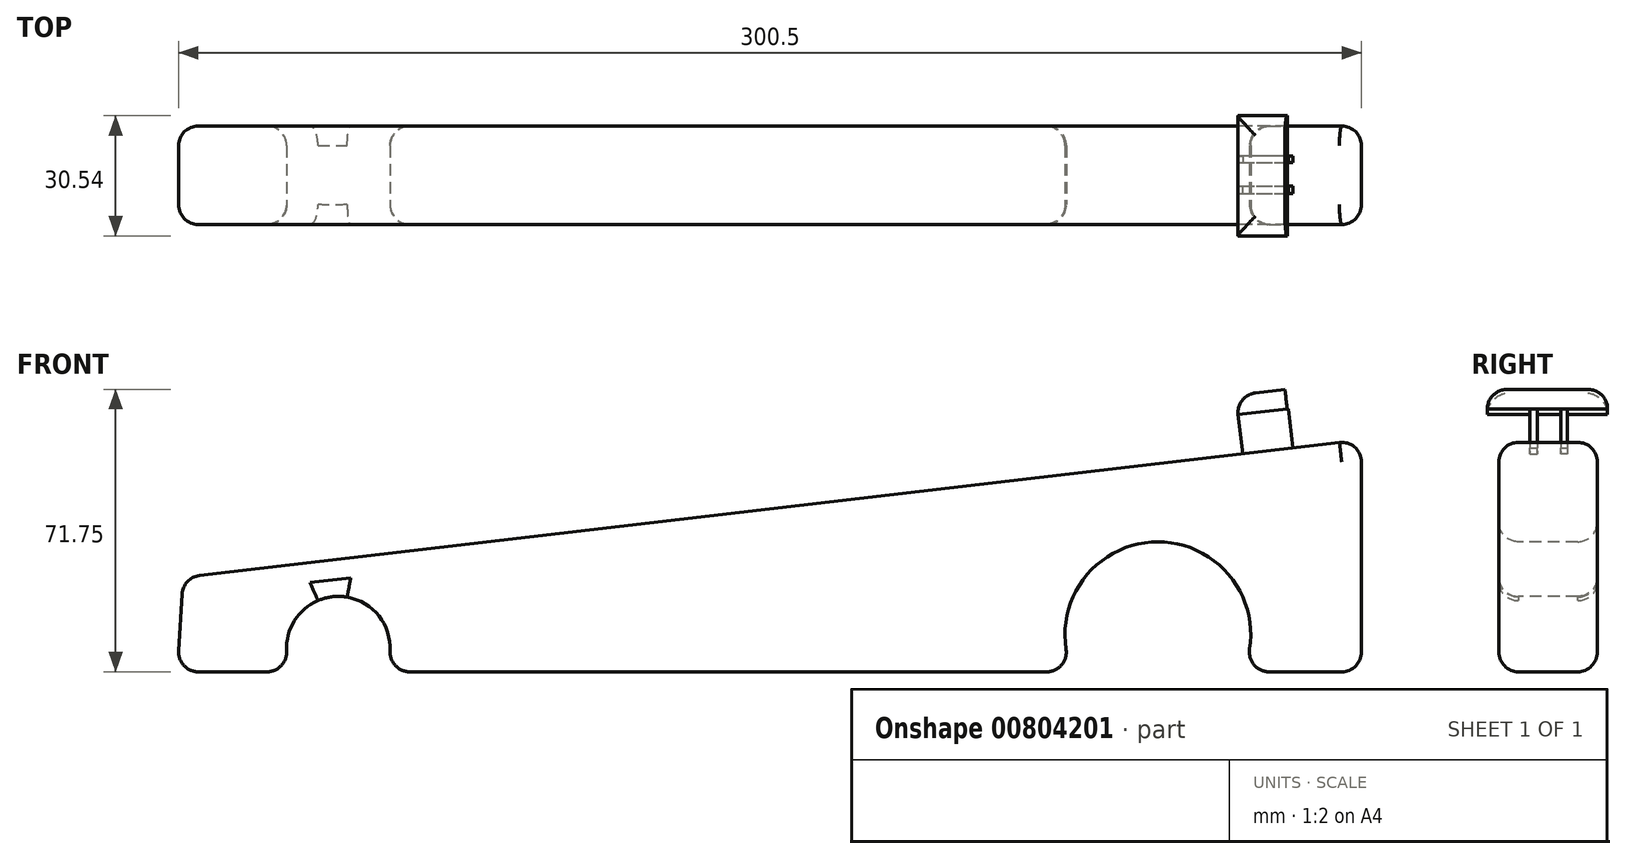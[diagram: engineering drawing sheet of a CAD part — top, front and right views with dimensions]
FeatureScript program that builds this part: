
annotation { "Feature Type Name" : "Feature", "Feature Type Description" : "" }
export const myFeature = defineFeature(function(context is Context, id is Id, definition is map)
    precondition{}
    {
        {
            var Q0;
            Q0=qCreatedBy(makeId("Front.planeOp"),FACE);
            var sketch = newSketch(context, id + "F0", { "sketchPlane" : qUnion([Q0])});
            skLineSegment(sketch, "E0", {"start": v(-173.6, -13.13) * mm, "end": v(127.2, -13.13) * mm});
            skLineSegment(sketch, "E1", {"start": v(127.2, -13.13) * mm, "end": v(127.2, 45.79) * mm});
            skLineSegment(sketch, "E2", {"start": v(127.2, 45.79) * mm, "end": v(-172.16, 10.82) * mm});
            skLineSegment(sketch, "E3", {"start": v(-172.16, 10.82) * mm, "end": v(-173.6, -13.13) * mm});
            skSolve(sketch);
        }
        {
            var Q0;
            Q0 = qSketchRegion(id + "F0", true);
            extrude(context, id + "F1", {"entities" : qUnion([Q0]), "depth" : 25 * mm, "offsetDistance" : 25 * mm});
        }
        {
            var Q0;
            Q0=makeQuery(id+"F1.opExtrude","CAP_EDGE",EDGE,{"disambiguationData":[OSD([sQuery(id+"F0.wireOp",EDGE,"E2")])],"isStart":false});
            var Q1;
            Q1=makeQuery(id+"F1.opExtrude","CAP_EDGE",EDGE,{"disambiguationData":[OSD([sQuery(id+"F0.wireOp",EDGE,"E1")])],"isStart":true});
            var Q2;
            Q2=makeQuery(id+"F1.opExtrude","CAP_EDGE",EDGE,{"disambiguationData":[OSD([sQuery(id+"F0.wireOp",EDGE,"E2")])],"isStart":true});
            var Q3;
            Q3=makeQuery(id+"F1.opExtrude","CAP_EDGE",EDGE,{"disambiguationData":[OSD([sQuery(id+"F0.wireOp",EDGE,"E1")])],"isStart":false});
            var Q4;
            Q4=makeQuery(id+"F1.opExtrude","CAP_EDGE",EDGE,{"disambiguationData":[OSD([sQuery(id+"F0.wireOp",EDGE,"E3")])],"isStart":false});
            var Q5;
            Q5=makeQuery(id+"F1.opExtrude","CAP_EDGE",EDGE,{"disambiguationData":[OSD([sQuery(id+"F0.wireOp",EDGE,"E3")])],"isStart":true});
            var Q6;
            Q6=makeQuery(id+"F1.opExtrude","SWEPT_EDGE",EDGE,{"disambiguationData":[OSD([sQuery(id+"F0.wireOp",EDGE,"E2"),sQuery(id+"F0.wireOp",EDGE,"E3")])]});
            fillet(context, id + "F2", {"entities" : qUnion([Q0, Q1, Q2, Q3, Q4, Q5, Q6]), "radius" : 5 * mm, "tangentPropagation" : true, "allowEdgeOverflow" : false});
        }
        {
            var Q0;
            Q0=makeQuery(id+"F1.opExtrude","SWEPT_EDGE",EDGE,{"disambiguationData":[OSD([sQuery(id+"F0.wireOp",EDGE,"E1"),sQuery(id+"F0.wireOp",EDGE,"E2")])]});
            fillet(context, id + "F3", {"entities" : qUnion([Q0]), "radius" : 5 * mm, "tangentPropagation" : true, "allowEdgeOverflow" : false});
        }
        {
            var Q0;
            Q0=makeQuery(id+"F1.opExtrude","CAP_FACE",FACE,{"disambiguationData":[OSD([sQuery(id+"F0.wireOp",EDGE,"E0"),sQuery(id+"F0.wireOp",EDGE,"E1"),sQuery(id+"F0.wireOp",EDGE,"E2"),sQuery(id+"F0.wireOp",EDGE,"E3")])],"isStart":false});
            var sketch = newSketch(context, id + "F4", { "sketchPlane" : qUnion([Q0])});
            skCircle(sketch, "E4", {"center": v(75.5, -3.7) * mm, "radius": 23.6 * mm});
            skCircle(sketch, "E5", {"center": v(-132.7, -7.12) * mm, "radius": 13.15 * mm});
            skSolve(sketch);
        }
        {
            var Q0;
            Q0 = qSketchRegion(id + "F4", true);
            extrude(context, id + "F5", {"entities" : qUnion([Q0]), "operationType" : NewBodyOperationType.REMOVE, "oppositeDirection" : true, "depth" : 25 * mm, "offsetDistance" : 25 * mm});
        }
        {
            var Q0;
            Q0=makeQuery(id+"F5.boolean.opBoolean","COPY",EDGE,{"derivedFrom":makeQuery(id+"F5.opExtrude","CAP_EDGE",EDGE,{"disambiguationData":[OSD([sQuery(id+"F4.wireOp",EDGE,"E5")])],"isStart":true})});
            var Q1;
            Q1=makeQuery(id+"F5.boolean.opBoolean","INTERSECT",EDGE,{"disambiguationData":[OD(0.0)],"derivedFrom":[makeQuery(id+"F1.opExtrude","SWEPT_FACE",FACE,{"disambiguationData":[OSD([sQuery(id+"F0.wireOp",EDGE,"E0")])]}),makeQuery(id+"F5.opExtrude","SWEPT_FACE",FACE,{"disambiguationData":[OSD([sQuery(id+"F4.wireOp",EDGE,"E5")])]})]});
            var Q2;
            {var subQ0=sQuery(id+"F0.wireOp",EDGE,"E0");Q2=makeQuery(id+"F5.boolean.opBoolean","SPLIT",EDGE,{"disambiguationData":[TD([makeQuery(id+"F1.opExtrude","SWEPT_FACE",FACE,{"disambiguationData":[OSD([subQ0])]}),makeQuery(id+"F1.opExtrude","CAP_FACE",FACE,{"disambiguationData":[OSD([subQ0,sQuery(id+"F0.wireOp",EDGE,"E1"),sQuery(id+"F0.wireOp",EDGE,"E2"),sQuery(id+"F0.wireOp",EDGE,"E3")])],"isStart":false}),makeQuery(id+"F5.opExtrude","SWEPT_FACE",FACE,{"disambiguationData":[OSD([sQuery(id+"F4.wireOp",EDGE,"E4")])]}),makeQuery(id+"F5.opExtrude","SWEPT_FACE",FACE,{"disambiguationData":[OSD([sQuery(id+"F4.wireOp",EDGE,"E5")])]})])],"derivedFrom":makeQuery(id+"F1.opExtrude","CAP_EDGE",EDGE,{"disambiguationData":[OSD([subQ0])],"isStart":false})});}
            var Q3;
            Q3=makeQuery(id+"F5.boolean.opBoolean","INTERSECT",EDGE,{"disambiguationData":[OD(1.0)],"derivedFrom":[makeQuery(id+"F1.opExtrude","SWEPT_FACE",FACE,{"disambiguationData":[OSD([sQuery(id+"F0.wireOp",EDGE,"E0")])]}),makeQuery(id+"F5.opExtrude","SWEPT_FACE",FACE,{"disambiguationData":[OSD([sQuery(id+"F4.wireOp",EDGE,"E4")])]})]});
            var Q4;
            Q4=makeQuery(id+"F5.boolean.opBoolean","COPY",EDGE,{"derivedFrom":makeQuery(id+"F5.opExtrude","CAP_EDGE",EDGE,{"disambiguationData":[OSD([sQuery(id+"F4.wireOp",EDGE,"E4")])],"isStart":true})});
            var Q5;
            Q5=makeQuery(id+"F5.boolean.opBoolean","INTERSECT",EDGE,{"disambiguationData":[OD(0.0)],"derivedFrom":[makeQuery(id+"F1.opExtrude","SWEPT_FACE",FACE,{"disambiguationData":[OSD([sQuery(id+"F0.wireOp",EDGE,"E0")])]}),makeQuery(id+"F5.opExtrude","SWEPT_FACE",FACE,{"disambiguationData":[OSD([sQuery(id+"F4.wireOp",EDGE,"E4")])]})]});
            var Q6;
            Q6=makeQuery(id+"F5.boolean.opBoolean","INTERSECT",EDGE,{"disambiguationData":[OD(1.0)],"derivedFrom":[makeQuery(id+"F1.opExtrude","SWEPT_FACE",FACE,{"disambiguationData":[OSD([sQuery(id+"F0.wireOp",EDGE,"E0")])]}),makeQuery(id+"F5.opExtrude","SWEPT_FACE",FACE,{"disambiguationData":[OSD([sQuery(id+"F4.wireOp",EDGE,"E5")])]})]});
            fillet(context, id + "F6", {"entities" : qUnion([Q0, Q1, Q2, Q3, Q4, Q5, Q6]), "radius" : 5 * mm, "tangentPropagation" : true, "allowEdgeOverflow" : false});
        }
        {
            var Q0;
            {var subQ0=sQuery(id+"F0.wireOp",EDGE,"E0");Q0=makeQuery(id+"F6.opFillet","BLEND_EDGE",EDGE,{"blendedFrom":[makeQuery(id+"F5.boolean.opBoolean","INTERSECT",EDGE,{"disambiguationData":[OD(0.0)],"derivedFrom":[makeQuery(id+"F1.opExtrude","SWEPT_FACE",FACE,{"disambiguationData":[OSD([subQ0])]}),makeQuery(id+"F5.opExtrude","SWEPT_FACE",FACE,{"disambiguationData":[OSD([sQuery(id+"F4.wireOp",EDGE,"E5")])]})]}),makeQuery(id+"F1.opExtrude","CAP_FACE",FACE,{"disambiguationData":[OSD([subQ0,sQuery(id+"F0.wireOp",EDGE,"E1"),sQuery(id+"F0.wireOp",EDGE,"E2"),sQuery(id+"F0.wireOp",EDGE,"E3")])],"isStart":true})],"blendedInto":[makeQuery(id+"F1.opExtrude","CAP_FACE",FACE,{"disambiguationData":[OSD([subQ0,sQuery(id+"F0.wireOp",EDGE,"E1"),sQuery(id+"F0.wireOp",EDGE,"E2"),sQuery(id+"F0.wireOp",EDGE,"E3")])],"isStart":true})]});}
            fillet(context, id + "F7", {"entities" : qUnion([Q0]), "radius" : 5 * mm, "tangentPropagation" : true, "allowEdgeOverflow" : false});
        }
        {
            var Q0;
            Q0=makeQuery(id+"F1.opExtrude","SWEPT_FACE",FACE,{"disambiguationData":[OSD([sQuery(id+"F0.wireOp",EDGE,"E2")])]});
            var sketch = newSketch(context, id + "F8", { "sketchPlane" : qUnion([Q0])});
            skLineSegment(sketch, "E6", {"start": v(101.3, -7.63) * mm, "end": v(101.3, -9.22) * mm});
            skLineSegment(sketch, "E7", {"start": v(101.3, -9.22) * mm, "end": v(114.14, -9.22) * mm});
            skLineSegment(sketch, "E8", {"start": v(114.14, -9.22) * mm, "end": v(114.14, -7.63) * mm});
            skLineSegment(sketch, "E9", {"start": v(114.14, -7.63) * mm, "end": v(101.3, -7.63) * mm});
            skLineSegment(sketch, "E10", {"start": v(101.3, -15.28) * mm, "end": v(114.14, -15.28) * mm});
            skLineSegment(sketch, "E11", {"start": v(114.14, -17.12) * mm, "end": v(114.14, -15.28) * mm});
            skLineSegment(sketch, "E12", {"start": v(101.3, -17.12) * mm, "end": v(101.3, -15.28) * mm});
            skLineSegment(sketch, "E13", {"start": v(101.3, -17.12) * mm, "end": v(114.14, -17.12) * mm});
            skSolve(sketch);
        }
        {
            var Q0;
            Q0 = qSketchRegion(id + "F8", true);
            extrude(context, id + "F9", {"entities" : qUnion([Q0]), "operationType" : NewBodyOperationType.ADD, "depth" : 10 * mm, "offsetDistance" : 25 * mm});
        }
        {
            var Q0;
            Q0=makeQuery(id+"F9.opExtrude","CAP_FACE",FACE,{"disambiguationData":[OSD([sQuery(id+"F8.wireOp",EDGE,"E10"),sQuery(id+"F8.wireOp",EDGE,"E11"),sQuery(id+"F8.wireOp",EDGE,"E12"),sQuery(id+"F8.wireOp",EDGE,"E13")])],"isStart":false});
            var sketch = newSketch(context, id + "F10", { "sketchPlane" : qUnion([Q0])});
            skLineSegment(sketch, "E14", {"start": v(101.3, -27.92) * mm, "end": v(101.3, 2.62) * mm});
            skLineSegment(sketch, "E15", {"start": v(101.3, 2.62) * mm, "end": v(113.85, 2.62) * mm});
            skLineSegment(sketch, "E16", {"start": v(113.85, 2.62) * mm, "end": v(113.85, -27.92) * mm});
            skLineSegment(sketch, "E17", {"start": v(113.85, -27.92) * mm, "end": v(101.3, -27.92) * mm});
            skSolve(sketch);
        }
        {
            var Q0;
            Q0 = qSketchRegion(id + "F10", true);
            extrude(context, id + "F11", {"entities" : qUnion([Q0]), "operationType" : NewBodyOperationType.ADD, "depth" : 5 * mm, "offsetDistance" : 25 * mm});
        }
        {
            var Q0;
            Q0=makeQuery(id+"F11.opExtrude","CAP_EDGE",EDGE,{"disambiguationData":[OSD([sQuery(id+"F10.wireOp",EDGE,"E17")])],"isStart":false});
            var Q1;
            Q1=makeQuery(id+"F11.opExtrude","CAP_EDGE",EDGE,{"disambiguationData":[OSD([sQuery(id+"F10.wireOp",EDGE,"E14")])],"isStart":false});
            var Q2;
            Q2=makeQuery(id+"F11.opExtrude","CAP_EDGE",EDGE,{"disambiguationData":[OSD([sQuery(id+"F10.wireOp",EDGE,"E15")])],"isStart":false});
            fillet(context, id + "F12", {"entities" : qUnion([Q0, Q1, Q2]), "radius" : 5 * mm, "tangentPropagation" : true, "allowEdgeOverflow" : false});
        }
    });
